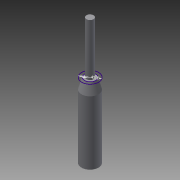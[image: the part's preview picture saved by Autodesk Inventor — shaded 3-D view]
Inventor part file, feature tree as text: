
AUTODESK INVENTOR PART (.ipt)
format: ipt  version: 2015 (Build 190159000, 159)  size: 82,944 bytes
history: native  units: mm
features: sketch x3, extrude x2, chamfer x1
ambient origin geometry x8: Origin, YZ Plane, XZ Plane, XY Plane, X Axis, Y Axis, Z Axis, Center Point
bodies: Solid1 (feature_tree)
feature tree (6):
  extrude  "Extrusion1"  Depth=53.4mm TaperAngle=0.0deg
  extrude  "Extrusion2"  Depth=22.0mm
  sketch  "Sketch3"  dims[d7=7.2mm d8=4.7mm d11=4.5mm d12=1.25mm d13=45.0deg]
  chamfer  "Chamfer1"  Distance=22.0mm
  sketch  "Sketch1"  dims[d0=7.2mm d1=53.4mm d2=0.0mm]
  sketch  "Sketch2"  dims[d3=3.0mm d4=7.2mm d5=22.0mm d6=0.0mm]
